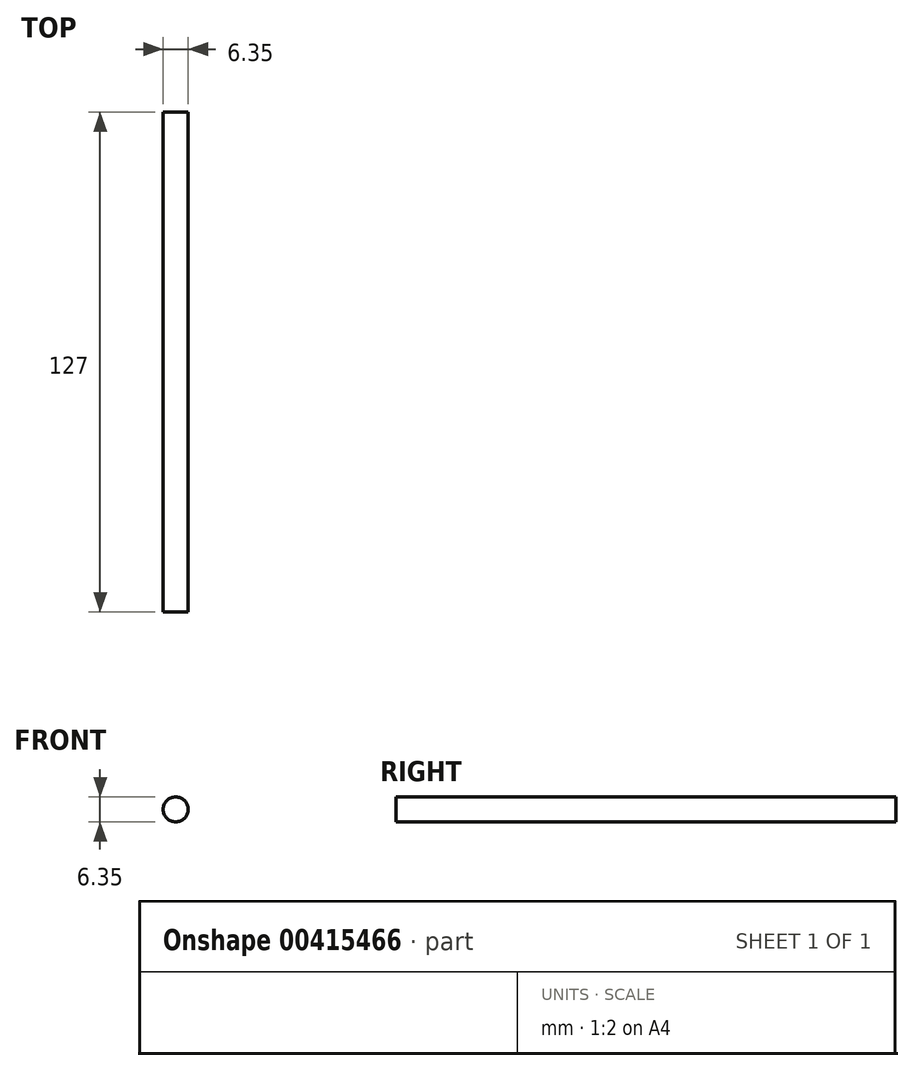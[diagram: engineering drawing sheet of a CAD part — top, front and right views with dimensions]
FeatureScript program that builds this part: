
annotation { "Feature Type Name" : "Feature", "Feature Type Description" : "" }
export const myFeature = defineFeature(function(context is Context, id is Id, definition is map)
    precondition{}
    {
        {
            var Q0;
            Q0=qCreatedBy(makeId("Front.planeOp"),FACE);
            var sketch = newSketch(context, id + "F0", { "sketchPlane" : qUnion([Q0])});
            skCircle(sketch, "E0", {"center": v(-40.3, 34.8) * mm, "radius": 3.18 * mm});
            skCircle(sketch, "E1", {"center": v(24.21, 35.57) * mm, "radius": 3.18 * mm});
            skCircle(sketch, "E2", {"center": v(-37.97, -19.1) * mm, "radius": 3.18 * mm});
            skSolve(sketch);
        }
        {
            var Q0;
            Q0=makeQuery(id+"F0.imprint","IMPRINT",FACE,{"disambiguationData":[TD([[makeQuery(id+"F0.imprint","IMPRINT",EDGE,{"derivedFrom":sQuery(id+"F0.wireOp",EDGE,"E0")}),1.0]])]});
            extrude(context, id + "F1", {"entities" : qUnion([Q0]), "depth" : 127 * mm, "offsetDistance" : 25.4 * mm});
        }
        {
            var Q0;
            Q0=sQuery(id+"F0.wireOp",EDGE,"E1");
            extrude(context, id + "F2", {"bodyType" : ToolBodyType.SURFACE, "surfaceEntities" : qUnion([Q0]), "depth" : 127 * mm, "offsetDistance" : 25.4 * mm});
        }
        {
            var Q0;
            Q0=sQuery(id+"F0.wireOp",EDGE,"E2");
            extrude(context, id + "F3", {"bodyType" : ToolBodyType.SURFACE, "surfaceEntities" : qUnion([Q0]), "depth" : 127 * mm, "offsetDistance" : 25.4 * mm});
        }
    });
